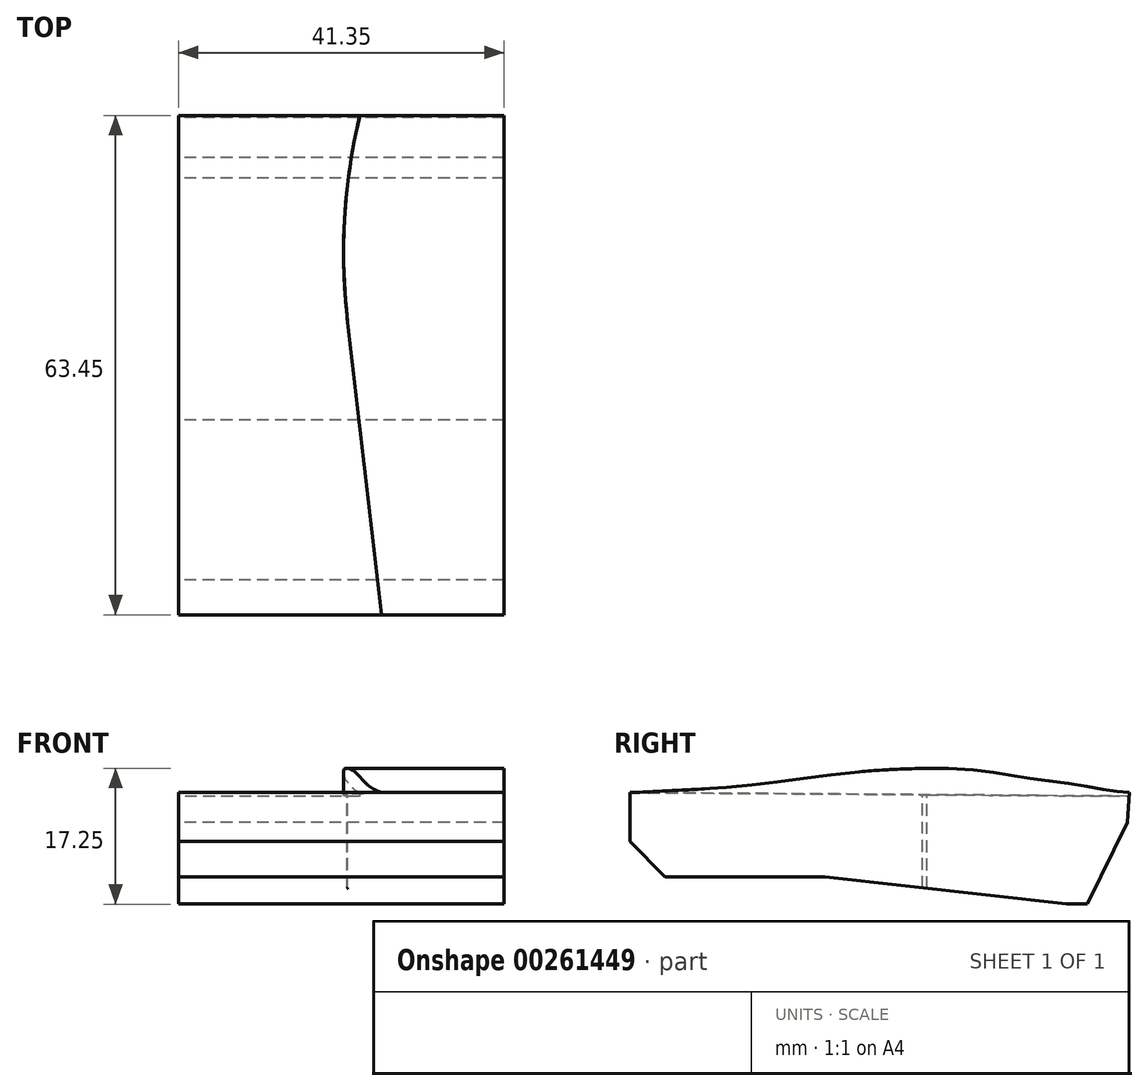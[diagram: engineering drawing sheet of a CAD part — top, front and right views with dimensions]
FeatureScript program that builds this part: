
annotation { "Feature Type Name" : "Feature", "Feature Type Description" : "" }
export const myFeature = defineFeature(function(context is Context, id is Id, definition is map)
    precondition{}
    {
        {
            var Q0;
            Q0=qCreatedBy(makeId("Right.planeOp"),FACE);
            var sketch = newSketch(context, id + "F0", { "sketchPlane" : qUnion([Q0])});
            skArc(sketch, "E0", {"start": v(39.53, -4.06) * mm, "mid": v(30.34, -7.1) * mm, "end": v(24.77, -15) * mm, "construction": true});
            skArc(sketch, "E1", {"start": v(55.46, -18.46) * mm, "mid": v(50.36, -8.09) * mm, "end": v(39.53, -4.06) * mm, "construction": true});
            skFitSpline(sketch, "E2", {"points": [v(63.45, -4.3) * mm, v(60.6, -3.94) * mm, v(55.65, -3.1) * mm, v(49.43, -2.27) * mm, v(43.3, -1.38) * mm, v(29.53, -1.62) * mm, v(17.15, -3.12) * mm, v(6.48, -3.98) * mm, v(0.43, -4.27) * mm, v(0, -4.3) * mm]});
            skLineSegment(sketch, "E3", {"start": v(4.44, -15) * mm, "end": v(24.77, -15) * mm});
            skLineSegment(sketch, "E4", {"start": v(55.46, -18.46) * mm, "end": v(58.1, -18.46) * mm});
            skLineSegment(sketch, "E5", {"start": v(58.1, -18.46) * mm, "end": v(63.18, -8.1) * mm});
            skLineSegment(sketch, "E6", {"start": v(63.18, -8.1) * mm, "end": v(63.45, -4.3) * mm});
            skLineSegment(sketch, "E7", {"start": v(4.44, -15) * mm, "end": v(0, -10.48) * mm});
            skLineSegment(sketch, "E8", {"start": v(0, -10.48) * mm, "end": v(0, -4.3) * mm});
            skLineSegment(sketch, "E9", {"start": v(24.77, -15) * mm, "end": v(55.46, -18.46) * mm});
            skSolve(sketch);
        }
        {
            var Q0;
            Q0=qSketchRegion(id+"F0",true);
            extrude(context, id + "F1", {"entities" : qUnion([Q0]), "depth" : 41.35 * mm});
        }
        {
            var Q0;
            Q0=qCreatedBy(makeId("Top.planeOp"),FACE);
            var sketch = newSketch(context, id + "F2", { "sketchPlane" : qUnion([Q0])});
            skFitSpline(sketch, "E10.0", {"points": [v(41.35, 63.45) * mm, v(41.35, 60.6) * mm, v(41.35, 55.65) * mm, v(41.35, 49.43) * mm, v(41.35, 43.3) * mm, v(41.35, 29.53) * mm, v(41.35, 17.15) * mm, v(41.35, 6.48) * mm, v(41.35, 0.43) * mm, v(41.35, 0) * mm], "construction": true});
            skLineSegment(sketch, "E11.0", {"start": v(25.8, 0) * mm, "end": v(0, 0) * mm});
            skLineSegment(sketch, "E12", {"start": v(25.8, 0) * mm, "end": v(21.43, 37.7) * mm});
            skArc(sketch, "E13", {"start": v(23.02, 63.45) * mm, "mid": v(21.1, 50.65) * mm, "end": v(21.43, 37.7) * mm});
            skLineSegment(sketch, "E14.trimOffspring", {"start": v(23.02, 63.45) * mm, "end": v(0, 63.45) * mm});
            skLineSegment(sketch, "E15", {"start": v(0, 0) * mm, "end": v(0, 63.45) * mm});
            skSolve(sketch);
        }
        {
            var Q0;
            Q0=qSketchRegion(id+"F2",true);
            extrude(context, id + "F3", {"entities" : qUnion([Q0]), "operationType" : NewBodyOperationType.REMOVE, "oppositeDirection" : true, "depth" : 25 * mm});
        }
        {
            var Q0;
            Q0=qCreatedBy(makeId("Right.planeOp"),FACE);
            var sketch = newSketch(context, id + "F4", { "sketchPlane" : qUnion([Q0])});
            skLineSegment(sketch, "E16.0", {"start": v(63.42, -4.75) * mm, "end": v(63.18, -8.1) * mm});
            skLineSegment(sketch, "E17.0", {"start": v(63.18, -8.1) * mm, "end": v(58.1, -18.46) * mm});
            skLineSegment(sketch, "E18.0", {"start": v(0, -10.48) * mm, "end": v(0, -4.3) * mm});
            skLineSegment(sketch, "E19.0", {"start": v(4.44, -15) * mm, "end": v(0, -10.48) * mm});
            skLineSegment(sketch, "E20.0", {"start": v(4.44, -15) * mm, "end": v(24.77, -15) * mm});
            skLineSegment(sketch, "E20.1", {"start": v(24.77, -15) * mm, "end": v(37.7, -16.46) * mm});
            skLineSegment(sketch, "E20.2", {"start": v(55.46, -18.46) * mm, "end": v(37.7, -16.46) * mm});
            skLineSegment(sketch, "E20.3", {"start": v(58.1, -18.46) * mm, "end": v(55.46, -18.46) * mm});
            skLineSegment(sketch, "E21", {"start": v(63.45, -4.3) * mm, "end": v(68.46, -4.3) * mm, "construction": true});
            skLineSegment(sketch, "E22.0", {"start": v(63.42, -4.75) * mm, "end": v(68.46, -4.75) * mm, "construction": true});
            skLineSegment(sketch, "E23", {"start": v(63.42, -4.75) * mm, "end": v(0, -4.3) * mm});
            skSolve(sketch);
        }
        {
            var Q0;
            Q0=qSketchRegion(id+"F4",true);
            var Q1;
            Q1=makeQuery(id+"F3.boolean.opBoolean","COPY",FACE,{"derivedFrom":makeQuery(id+"F3.opExtrude","SWEPT_FACE",FACE,{"disambiguationData":[OSD([sQuery(id+"F2.wireOp",EDGE,"E13")])]})});
            extrude(context, id + "F5", {"entities" : qUnion([Q0]), "operationType" : NewBodyOperationType.ADD, "endBound" : BoundingType.UP_TO_SURFACE, "endBoundEntityFace" : qUnion([Q1]), "depth" : 25 * mm});
        }
        {
            var Q0;
            Q0=qCreatedBy(makeId("Front.planeOp"),FACE);
            var sketch = newSketch(context, id + "F6", { "sketchPlane" : qUnion([Q0])});
            skLineSegment(sketch, "E24.0", {"start": v(20.88, -4.3) * mm, "end": v(0, -4.3) * mm});
            skLineSegment(sketch, "E25", {"start": v(0, -4.3) * mm, "end": v(0, 6.72) * mm});
            skLineSegment(sketch, "E26.0", {"start": v(20.88, 6.72) * mm, "end": v(0, 6.72) * mm, "construction": true});
            skLineSegment(sketch, "E27.0", {"start": v(20.88, -4.3) * mm, "end": v(20.88, 6.72) * mm, "construction": true});
            skPoint(sketch, "E28.orphan", {"position": v(25.8, -4.3) * mm});
            skLineSegment(sketch, "E29.0", {"start": v(20.88, 6.23) * mm, "end": v(9.22, 6.23) * mm, "construction": true});
            skLineSegment(sketch, "E30.0", {"start": v(9.22, -4.3) * mm, "end": v(9.22, 6.23) * mm, "construction": true});
            skArc(sketch, "E31", {"start": v(9.22, 6.23) * mm, "mid": v(4.61, 6.57) * mm, "end": v(0, 6.72) * mm});
            skLineSegment(sketch, "E32.0", {"start": v(20.88, 3.8) * mm, "end": v(15.26, 3.8) * mm, "construction": true});
            skLineSegment(sketch, "E33.0", {"start": v(15.26, -4.3) * mm, "end": v(15.26, 3.8) * mm, "construction": true});
            skArc(sketch, "E34", {"start": v(15.26, 3.8) * mm, "mid": v(12.42, 5.45) * mm, "end": v(9.22, 6.23) * mm});
            skArc(sketch, "E35", {"start": v(20.88, -4.3) * mm, "mid": v(18.54, 0.08) * mm, "end": v(15.26, 3.8) * mm});
            skSolve(sketch);
        }
        {
            var Q0;
            Q0=makeQuery(id+"F5.opExtrude","SWEPT_FACE",FACE,{"disambiguationData":[OSD([sQuery(id+"F4.wireOp",EDGE,"E23")])]});
            cPlane(context, id + "F7", {"entities" : qUnion([Q0]), "cplaneType" : CPlaneType.OFFSET, "offset" : 0 * mm, "width" : 150 * mm, "height" : 150 * mm});
        }
    });
